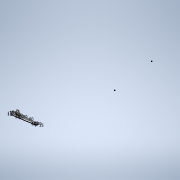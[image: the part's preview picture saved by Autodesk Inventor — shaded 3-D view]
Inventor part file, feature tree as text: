
AUTODESK INVENTOR PART (.ipt)
format: ipt  version: 2020.3 (Build 243373000, 373)  size: 241,152 bytes
history: native  units: mm
features: fillet x5, hole x3, sketch x2, extrude x2, chamfer x1
ambient origin geometry x8: Origin, YZ Plane, XZ Plane, XY Plane, X Axis, Y Axis, Z Axis, Center Point
bodies: Solid1 (feature_tree)
feature tree (13):
  sketch  "Sketch1"  dims[d4=5.0mm d5=23.0mm]
  extrude  "Extrusion1"  Depth=23.0mm
  chamfer  "Chamfer1"  Distance=5.0mm
  fillet  "Fillet1"  Radius=7.0mm
  fillet  "Fillet2"  Radius=5.0mm
  fillet  "Fillet3"  Radius=4.0mm
  fillet  "Fillet4"  Radius=20.0mm
  hole  "Hole3"  [1 undecoded]
  hole  "Hole4"  [1 undecoded]
  extrude  "Extrusion3"  Depth=5.0mm
  fillet  "Fillet6"  Radius=6.0mm
  hole  "Hole5"  [1 undecoded]
  sketch  "Sketch2"  dims[d6=13.0mm d7=5.0mm d15=7.0mm d17=5.0mm d18=4.0mm d21=20.0mm d23=80.0mm d24=15.0mm d29=29.670597mm d30=6.0mm d31=10.0mm d33=6.0mm d34=0.0mm d37=2.5mm d38=2.0mm d39=45.0deg d40=3.0mm d41=3.0mm d42=2.0mm d43=4.0mm d44=3.0mm d45=4.0mm d50=13.0mm d51=12.0mm d52=22.68928mm d53=16.057029mm d61=0.5mm d69=2.0mm d70=6.0mm d71=4.0mm d72=2.0mm d73=90.0deg d74=5.0mm d75=20.594885mm d76=2.0mm d77=6.0mm d78=4.0mm d79=2.0mm d80=90.0deg d81=5.0mm d82=20.594885mm d83=15.0mm d84=0.0mm d86=2.0mm d87=5.0mm d88=2.0mm d89=6.0mm d90=4.0mm d91=2.0mm d92=90.0deg d93=5.0mm d94=20.594885mm]
note: 3 required parameter values undecoded (feature->parameter linkage not recoverable at this tier; creation-order binding heuristic only, values carry confidence <= 0.55)
